SOLIDWORKS PART (.sldprt)
format: sldprt  version: not decoded by parser v0  size: 111,616 bytes
history: native  units: mm
features: sketch x2, extrude x2, material x1, fillet x1, mirror x1 (+13 scaffold rows collapsed)
feature tree (20):
  scaffold x13  (default folders/planes/origin — collapsed)
  material  "Material <not specified>"
  sketch  "Sketch1"  dims[c1.D1=6.0mm c1.D2=~26.72494mm c2.D2=135.0deg c3.D2=~9.153915mm c3.D3=~37.807831mm c3.D4=19.5mm c3.D5=~25.432299mm c4.D5=90.0deg c5.D5=3.0mm c5.D6=2.0]
  extrude  "Boss-Extrude1"  Depth=8mm
  fillet  "Fillet1"  Radius=10mm
  sketch  "Sketch3"  dims[D1=19.5mm]
  extrude  "Boss-Extrude2"  Depth=9mm
  mirror  "Mirror1"
decode coverage: 5 of 6 modeling features carry decoded parameters
note: ~ marks probable driven/reference dimensions
note: suppression state not decoded; provenance and decode notes live in map.json
